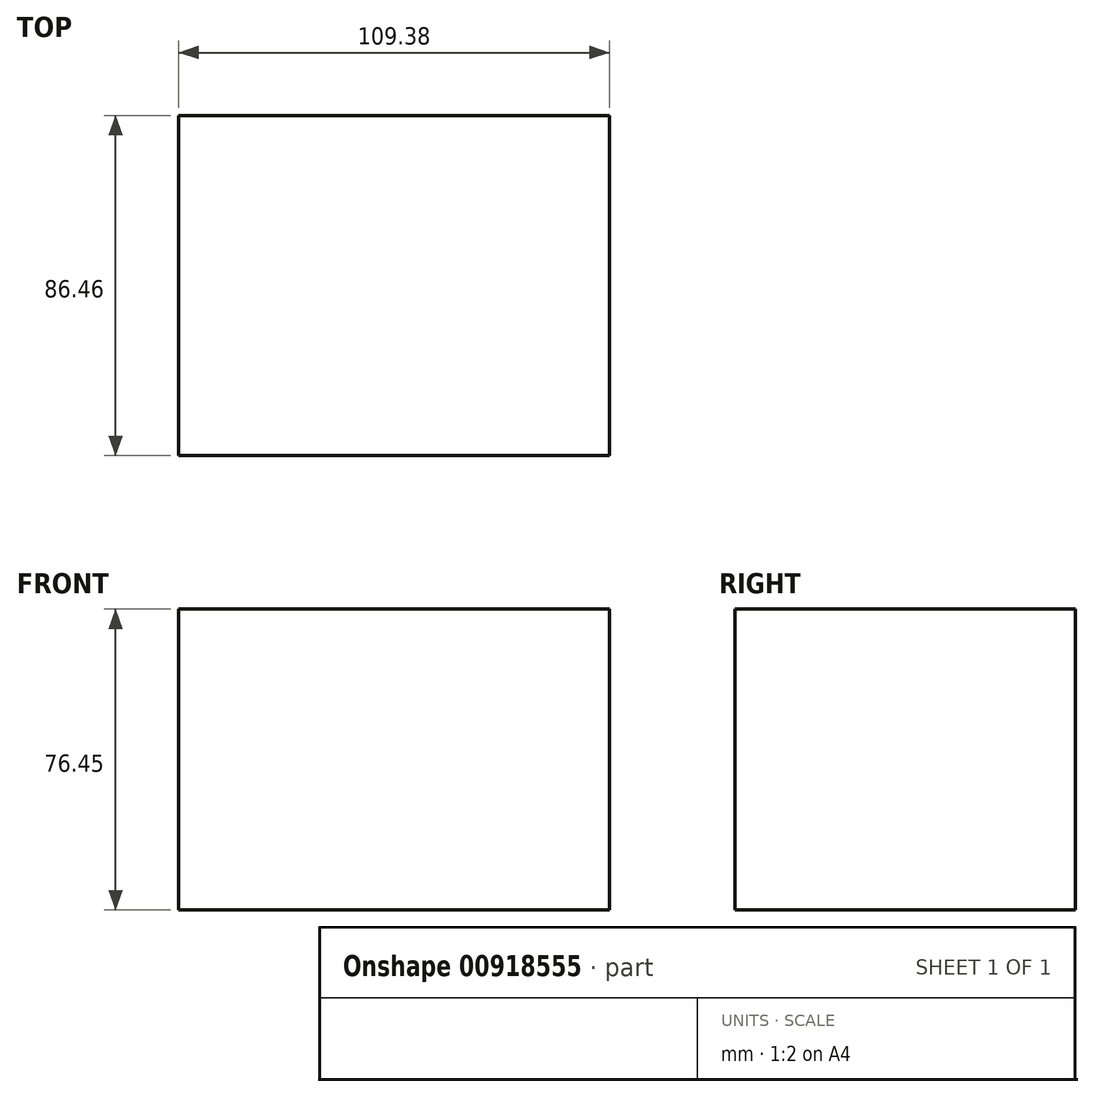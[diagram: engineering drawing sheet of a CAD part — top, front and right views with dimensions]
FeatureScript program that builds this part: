
annotation { "Feature Type Name" : "Feature", "Feature Type Description" : "" }
export const myFeature = defineFeature(function(context is Context, id is Id, definition is map)
    precondition{}
    {
        {
            var Q0;
            Q0=qCreatedBy(makeId("Top.planeOp"),FACE);
            var sketch = newSketch(context, id + "F0", { "sketchPlane" : qUnion([Q0])});
            skLineSegment(sketch, "E0.bottom", {"start": v(-59.26, -48.03) * mm, "end": v(50.12, -48.03) * mm});
            skLineSegment(sketch, "E0.top", {"start": v(-59.26, 38.43) * mm, "end": v(50.12, 38.43) * mm});
            skLineSegment(sketch, "E0.left", {"start": v(-59.26, -48.03) * mm, "end": v(-59.26, 38.43) * mm});
            skLineSegment(sketch, "E0.right", {"start": v(50.12, -48.03) * mm, "end": v(50.12, 38.43) * mm});
            skSolve(sketch);
        }
        {
            var Q0;
            Q0=makeQuery(id+"F0.imprint","IMPRINT",FACE,{"disambiguationData":[TD([[makeQuery(id+"F0.imprint","IMPRINT",EDGE,{"derivedFrom":sQuery(id+"F0.wireOp",EDGE,"E0.bottom")}),1.0]])]});
            extrude(context, id + "F1", {"entities" : qUnion([Q0]), "depth" : 76.45 * mm, "offsetDistance" : 25.4 * mm});
        }
    });
